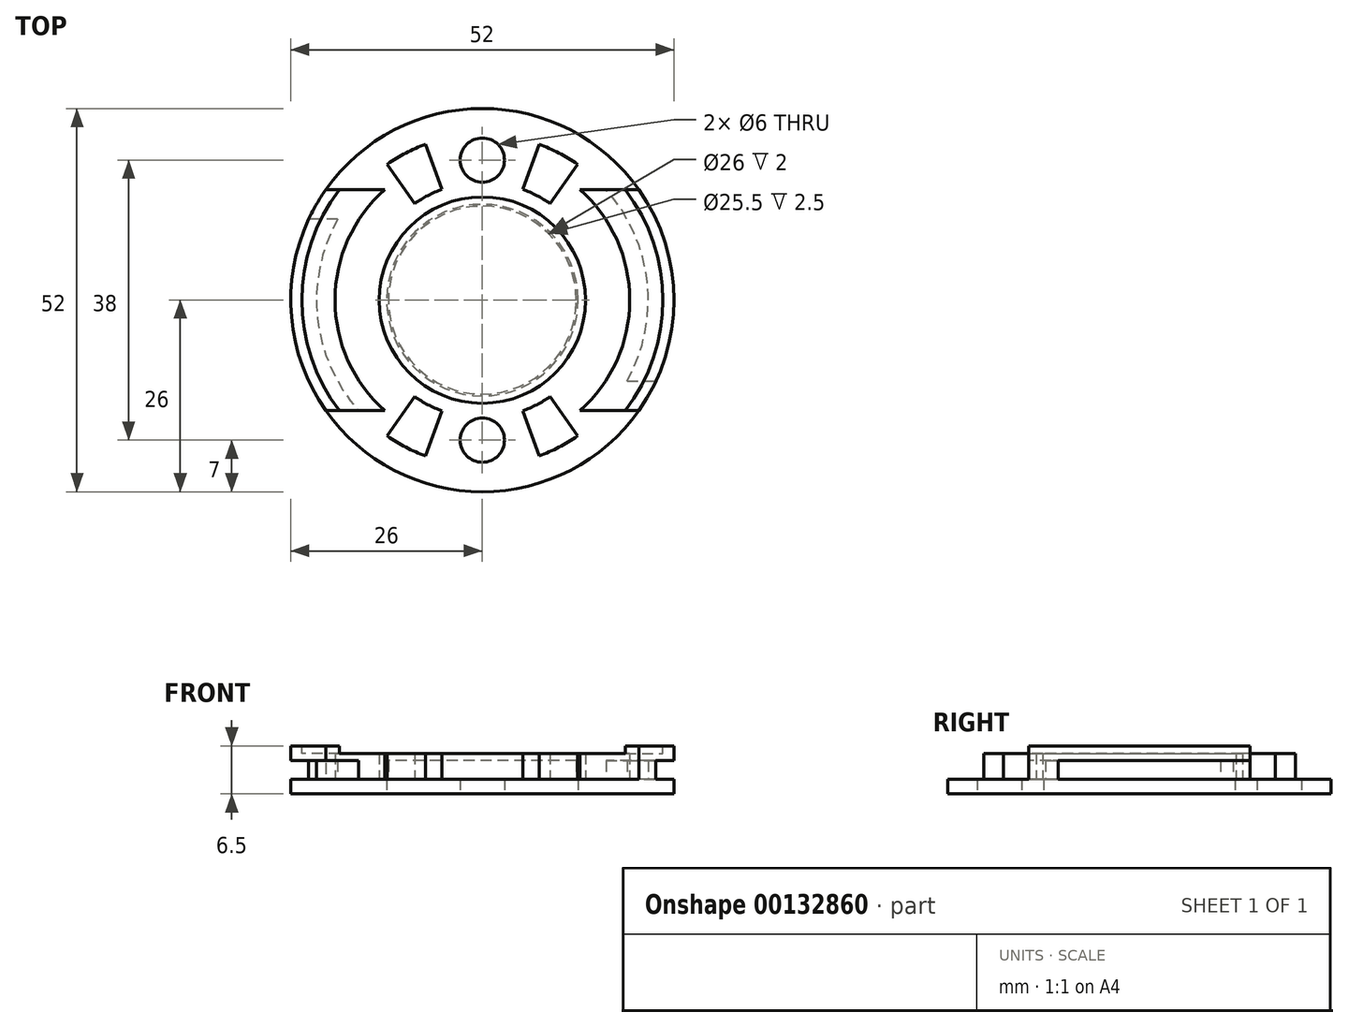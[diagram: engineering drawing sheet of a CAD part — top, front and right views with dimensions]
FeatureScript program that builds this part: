
annotation { "Feature Type Name" : "Feature", "Feature Type Description" : "" }
export const myFeature = defineFeature(function(context is Context, id is Id, definition is map)
    precondition{}
    {
        {
            var Q0;
            Q0=qCreatedBy(makeId("Top.planeOp"),FACE);
            var sketch = newSketch(context, id + "F0", { "sketchPlane" : qUnion([Q0])});
            skCircle(sketch, "E0", {"center": v(0, 0) * mm, "radius": 13 * mm});
            skArc(sketch, "E1", {"start": v(-15, -21.24) * mm, "mid": v(0, -26) * mm, "end": v(15, -21.24) * mm});
            skArc(sketch, "E2.trimOffspring", {"start": v(15, 21.24) * mm, "mid": v(0, 26) * mm, "end": v(-15, 21.24) * mm});
            skCircle(sketch, "E3", {"center": v(0, 19) * mm, "radius": 3 * mm});
            skCircle(sketch, "E4", {"center": v(0, -19) * mm, "radius": 3 * mm});
            skArc(sketch, "E5", {"start": v(-15, 21.24) * mm, "mid": v(-26, 0) * mm, "end": v(-15, -21.24) * mm});
            skArc(sketch, "E6.trimOffspring", {"start": v(15, -21.24) * mm, "mid": v(26, 0) * mm, "end": v(15, 21.24) * mm});
            skSolve(sketch);
        }
        {
            var Q0;
            Q0 = qSketchRegion(id + "F0", true);
            extrude(context, id + "F1", {"entities" : qUnion([Q0]), "depth" : 2 * mm, "offsetDistance" : 25 * mm});
        }
        {
            var Q0;
            Q0=makeQuery(id+"F1.opExtrude","CAP_FACE",FACE,{"disambiguationData":[OSD([sQuery(id+"F0.wireOp",EDGE,"E0"),sQuery(id+"F0.wireOp",EDGE,"E1"),sQuery(id+"F0.wireOp",EDGE,"kTxjDZJm-07je-H4XC-RKyD-XaX3gDPw2bY0.left"),sQuery(id+"F0.wireOp",EDGE,"kTxjDZJm-07je-H4XC-RKyD-XaX3gDPw2bY0.right"),sQuery(id+"F0.wireOp",EDGE,"E2.trimOffspring"),sQuery(id+"F0.wireOp",EDGE,"E3"),sQuery(id+"F0.wireOp",EDGE,"E4")])],"isStart":false});
            var sketch = newSketch(context, id + "F2", { "sketchPlane" : qUnion([Q0])});
            skCircle(sketch, "E7", {"center": v(0, 0) * mm, "radius": 12.75 * mm});
            skCircle(sketch, "E8", {"center": v(0, 0) * mm, "radius": 14 * mm});
            skSolve(sketch);
        }
        {
            var Q0;
            Q0 = qSketchRegion(id + "F2", true);
            extrude(context, id + "F3", {"entities" : qUnion([Q0]), "operationType" : NewBodyOperationType.ADD, "depth" : 2.5 * mm, "offsetDistance" : 25 * mm});
        }
        {
            var Q0;
            Q0=makeQuery(id+"F3.opExtrude","CAP_FACE",FACE,{"disambiguationData":[OSD([sQuery(id+"F2.wireOp",EDGE,"E7"),sQuery(id+"F2.wireOp",EDGE,"E8")])],"isStart":false});
            var sketch = newSketch(context, id + "F4", { "sketchPlane" : qUnion([Q0])});
            skCircle(sketch, "E9", {"center": v(0, 0) * mm, "radius": 14 * mm});
            skSolve(sketch);
        }
        {
            var Q0;
            Q0 = qSketchRegion(id + "F4", true);
            extrude(context, id + "F5", {"entities" : qUnion([Q0]), "operationType" : NewBodyOperationType.ADD, "depth" : 2 * mm, "offsetDistance" : 25 * mm});
        }
        {
            var Q0;
            Q0=makeQuery(id+"F1.opExtrude","CAP_FACE",FACE,{"disambiguationData":[OSD([sQuery(id+"F0.wireOp",EDGE,"E0"),sQuery(id+"F0.wireOp",EDGE,"E1"),sQuery(id+"F0.wireOp",EDGE,"E2.trimOffspring"),sQuery(id+"F0.wireOp",EDGE,"E3"),sQuery(id+"F0.wireOp",EDGE,"E4"),sQuery(id+"F0.wireOp",EDGE,"E5"),sQuery(id+"F0.wireOp",EDGE,"E6.trimOffspring")])],"isStart":false});
            var sketch = newSketch(context, id + "F6", { "sketchPlane" : qUnion([Q0])});
            skArc(sketch, "E10", {"start": v(19.63, -11) * mm, "mid": v(22.37, 2.46) * mm, "end": v(16.77, 15) * mm});
            skArc(sketch, "E11", {"start": v(13.23, -15) * mm, "mid": v(20, 0) * mm, "end": v(13.23, 15) * mm});
            skLineSegment(sketch, "E12.bottom", {"start": v(-16.77, 15) * mm, "end": v(-13.23, 15) * mm});
            skLineSegment(sketch, "E12.top", {"start": v(-16.77, -15) * mm, "end": v(-13.23, -15) * mm});
            skLineSegment(sketch, "E13.trimOffspring", {"start": v(13.23, -15) * mm, "end": v(16.77, -15) * mm});
            skLineSegment(sketch, "E14.trimOffspring", {"start": v(13.23, 15) * mm, "end": v(16.77, 15) * mm});
            skArc(sketch, "E15.trimOffspring", {"start": v(-13.23, 15) * mm, "mid": v(-20, 0) * mm, "end": v(-13.23, -15) * mm});
            skArc(sketch, "E16.trimOffspring", {"start": v(-19.63, 11) * mm, "mid": v(-22.37, -2.46) * mm, "end": v(-16.77, -15) * mm});
            skLineSegment(sketch, "E17", {"start": v(16.77, -15) * mm, "end": v(21.24, -15) * mm});
            skLineSegment(sketch, "E18", {"start": v(19.63, -11) * mm, "end": v(23.56, -11) * mm});
            skArc(sketch, "E19", {"start": v(21.24, -15) * mm, "mid": v(22.49, -13.05) * mm, "end": v(23.56, -11) * mm});
            skLineSegment(sketch, "E20", {"start": v(-16.77, 15) * mm, "end": v(-21.24, 15) * mm});
            skLineSegment(sketch, "E21", {"start": v(-19.63, 11) * mm, "end": v(-23.56, 11) * mm});
            skArc(sketch, "E22.trimOffspring", {"start": v(-21.24, 15) * mm, "mid": v(-22.49, 13.05) * mm, "end": v(-23.56, 11) * mm});
            skSolve(sketch);
        }
        {
            var Q0;
            Q0 = qSketchRegion(id + "F6", true);
            extrude(context, id + "F7", {"entities" : qUnion([Q0]), "operationType" : NewBodyOperationType.ADD, "depth" : 2.5 * mm, "offsetDistance" : 25 * mm});
        }
        {
            var Q0;
            Q0=makeQuery(id+"F7.opExtrude","CAP_FACE",FACE,{"disambiguationData":[OSD([sQuery(id+"F6.wireOp",EDGE,"E12.bottom"),sQuery(id+"F6.wireOp",EDGE,"E12.top"),sQuery(id+"F6.wireOp",EDGE,"E15.trimOffspring"),sQuery(id+"F6.wireOp",EDGE,"E16.trimOffspring"),sQuery(id+"F6.wireOp",EDGE,"E20"),sQuery(id+"F6.wireOp",EDGE,"E21"),sQuery(id+"F6.wireOp",EDGE,"E22.trimOffspring")])],"isStart":false});
            var sketch = newSketch(context, id + "F8", { "sketchPlane" : qUnion([Q0])});
            skArc(sketch, "E23", {"start": v(-21.24, 15) * mm, "mid": v(-26, 0) * mm, "end": v(-21.24, -15) * mm});
            skArc(sketch, "E24", {"start": v(-13.23, 15) * mm, "mid": v(-20, 0) * mm, "end": v(-13.23, -15) * mm});
            skLineSegment(sketch, "E25", {"start": v(-13.23, 15) * mm, "end": v(-21.24, 15) * mm});
            skLineSegment(sketch, "E26", {"start": v(-13.23, -15) * mm, "end": v(-21.24, -15) * mm});
            skLineSegment(sketch, "E27", {"start": v(0, 40.4) * mm, "end": v(0, -32.7) * mm, "construction": true});
            skArc(sketch, "E28.MirrorCS", {"start": v(21.24, 15) * mm, "mid": v(26, 0) * mm, "end": v(21.24, -15) * mm});
            skArc(sketch, "E29.MirrorCS", {"start": v(13.23, 15) * mm, "mid": v(20, 0) * mm, "end": v(13.23, -15) * mm});
            skLineSegment(sketch, "E30.MirrorCS", {"start": v(13.23, -15) * mm, "end": v(21.24, -15) * mm});
            skLineSegment(sketch, "E31.MirrorCS", {"start": v(13.23, 15) * mm, "end": v(21.24, 15) * mm});
            skSolve(sketch);
        }
        {
            var Q0;
            Q0 = qSketchRegion(id + "F8", true);
            extrude(context, id + "F9", {"entities" : qUnion([Q0]), "operationType" : NewBodyOperationType.ADD, "depth" : 2 * mm});
        }
        {
            var Q0;
            Q0=makeQuery(id+"F1.opExtrude","CAP_FACE",FACE,{"disambiguationData":[OSD([sQuery(id+"F0.wireOp",EDGE,"E0"),sQuery(id+"F0.wireOp",EDGE,"E1"),sQuery(id+"F0.wireOp",EDGE,"E2.trimOffspring"),sQuery(id+"F0.wireOp",EDGE,"E3"),sQuery(id+"F0.wireOp",EDGE,"E4"),sQuery(id+"F0.wireOp",EDGE,"E5"),sQuery(id+"F0.wireOp",EDGE,"E6.trimOffspring")])],"isStart":false});
            var sketch = newSketch(context, id + "F10", { "sketchPlane" : qUnion([Q0])});
            skLineSegment(sketch, "E32", {"start": v(-5.47, 15.04) * mm, "end": v(-7.7, 21.14) * mm});
            skLineSegment(sketch, "E33", {"start": v(-12.9, 18.43) * mm, "end": v(-9.18, 13.1) * mm});
            skArc(sketch, "E34", {"start": v(-7.7, 21.14) * mm, "mid": v(-10.39, 19.96) * mm, "end": v(-12.9, 18.43) * mm});
            skArc(sketch, "E35", {"start": v(-5.47, 15.04) * mm, "mid": v(-7.39, 14.2) * mm, "end": v(-9.18, 13.1) * mm});
            skLineSegment(sketch, "E36", {"start": v(0, 42.2) * mm, "end": v(0, -32.72) * mm, "construction": true});
            skLineSegment(sketch, "E37", {"start": v(56.1, 0) * mm, "end": v(-38.27, 0) * mm, "construction": true});
            skArc(sketch, "E38.MirrorCS", {"start": v(5.47, 15.04) * mm, "mid": v(7.39, 14.2) * mm, "end": v(9.18, 13.1) * mm});
            skLineSegment(sketch, "E39.MirrorCS", {"start": v(5.47, 15.04) * mm, "end": v(7.7, 21.14) * mm});
            skLineSegment(sketch, "E40.MirrorCS", {"start": v(12.9, 18.43) * mm, "end": v(9.18, 13.1) * mm});
            skArc(sketch, "E41.MirrorCS", {"start": v(7.7, 21.14) * mm, "mid": v(10.39, 19.96) * mm, "end": v(12.9, 18.43) * mm});
            skArc(sketch, "E42.MirrorCS", {"start": v(-5.47, -15.04) * mm, "mid": v(-7.39, -14.2) * mm, "end": v(-9.18, -13.1) * mm});
            skArc(sketch, "E43.MirrorCS", {"start": v(5.47, -15.04) * mm, "mid": v(7.39, -14.2) * mm, "end": v(9.18, -13.1) * mm});
            skArc(sketch, "E44.MirrorCS", {"start": v(-7.7, -21.14) * mm, "mid": v(-10.39, -19.96) * mm, "end": v(-12.9, -18.43) * mm});
            skLineSegment(sketch, "E45.MirrorCS", {"start": v(5.47, -15.04) * mm, "end": v(7.7, -21.14) * mm});
            skLineSegment(sketch, "E46.MirrorCS", {"start": v(-12.9, -18.43) * mm, "end": v(-9.18, -13.1) * mm});
            skLineSegment(sketch, "E47.MirrorCS", {"start": v(12.9, -18.43) * mm, "end": v(9.18, -13.1) * mm});
            skLineSegment(sketch, "E48.MirrorCS", {"start": v(-5.47, -15.04) * mm, "end": v(-7.7, -21.14) * mm});
            skArc(sketch, "E49.MirrorCS", {"start": v(7.7, -21.14) * mm, "mid": v(10.39, -19.96) * mm, "end": v(12.9, -18.43) * mm});
            skSolve(sketch);
        }
        {
            var Q0;
            Q0 = qSketchRegion(id + "F10", true);
            extrude(context, id + "F11", {"entities" : qUnion([Q0]), "operationType" : NewBodyOperationType.ADD, "depth" : 4.5 * mm});
        }
        {
            var Q0;
            Q0=makeQuery(id+"F5.opExtrude","CAP_FACE",FACE,{"disambiguationData":[OSD([sQuery(id+"F4.wireOp",EDGE,"E9")])],"isStart":false});
            var sketch = newSketch(context, id + "F12", { "sketchPlane" : qUnion([Q0])});
            skCircle(sketch, "E50", {"center": v(0, 0) * mm, "radius": 24.5 * mm});
            skSolve(sketch);
        }
        {
            var Q0;
            Q0 = qSketchRegion(id + "F12", true);
            extrude(context, id + "F13", {"entities" : qUnion([Q0]), "operationType" : NewBodyOperationType.REMOVE, "oppositeDirection" : true, "depth" : 1 * mm, "offsetDistance" : 25 * mm});
        }
    });
